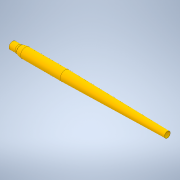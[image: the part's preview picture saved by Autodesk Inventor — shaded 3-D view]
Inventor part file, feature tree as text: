
AUTODESK INVENTOR PART (.ipt)
format: ipt  version: 2022 (Build 260153000, 153)  size: 141,824 bytes
history: native  units: mm
features: sketch x1, other x1, revolve x1
ambient origin geometry x8: Origin, YZ Plane, XZ Plane, XY Plane, X Axis, Y Axis, Z Axis, Center Point
bodies: Body1 (feature_tree)
feature tree (3):
  sketch  "Sketch1"  dims[d0=20.0mm d1=90.0deg d2=40.0mm d3=20.0mm d4=20.0mm d5=27.5mm d6=45.0mm d7=27.5mm d8=200.0mm d9=27.5mm d10=595.0mm d11=180.0deg d12=16.0mm d13=90.0deg d14=21.0mm d15=21.0mm d16=28.5mm d17=28.5mm d18=28.5mm d19=17.0mm d20=90.0deg d21=180.0deg d22=30.0mm d23=30.0mm d24=80.0mm d25=80.0mm]
  other  "Srf1"
  revolve  "RevolutionSrf1"  Angle=90.0deg
